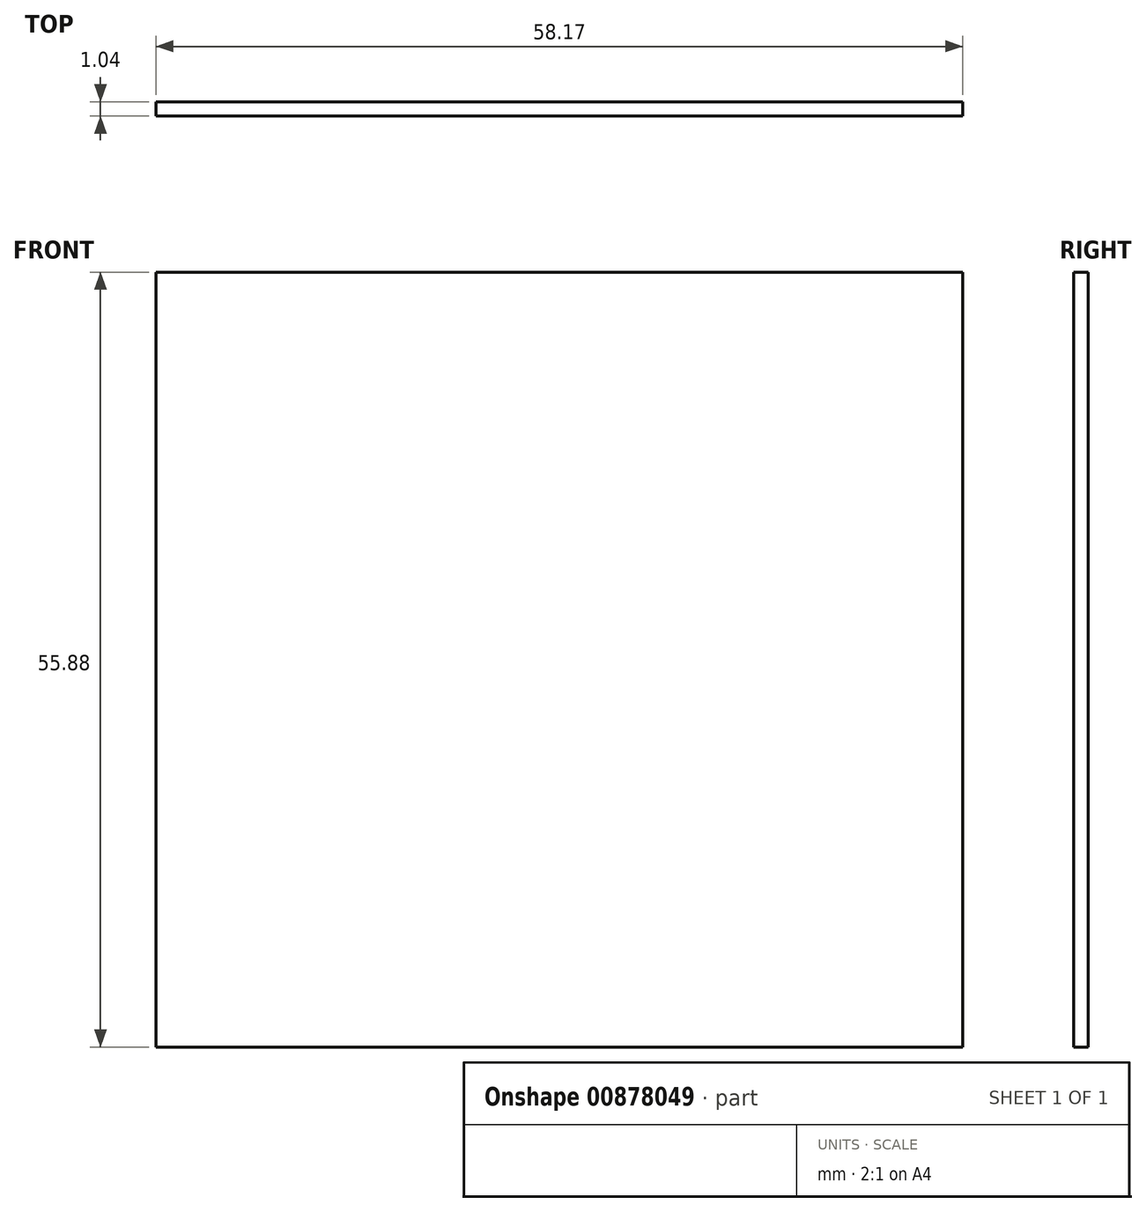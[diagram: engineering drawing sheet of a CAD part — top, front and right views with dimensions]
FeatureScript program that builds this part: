
annotation { "Feature Type Name" : "Feature", "Feature Type Description" : "" }
export const myFeature = defineFeature(function(context is Context, id is Id, definition is map)
    precondition{}
    {
        {
            var Q0;
            Q0=qCreatedBy(makeId("Front.planeOp"),FACE);
            var sketch = newSketch(context, id + "F0", { "sketchPlane" : qUnion([Q0])});
            skLineSegment(sketch, "E0.bottom", {"start": v(0, 0) * mm, "end": v(58.17, 0) * mm});
            skLineSegment(sketch, "E0.top", {"start": v(0, 55.88) * mm, "end": v(58.17, 55.88) * mm});
            skLineSegment(sketch, "E0.left", {"start": v(0, 0) * mm, "end": v(0, 55.88) * mm});
            skLineSegment(sketch, "E0.right", {"start": v(58.17, 0) * mm, "end": v(58.17, 55.88) * mm});
            skSolve(sketch);
        }
        {
            var Q0;
            Q0 = qSketchRegion(id + "F0", true);
            extrude(context, id + "F1", {"entities" : qUnion([Q0]), "depth" : 1.04 * mm, "offsetDistance" : 25.4 * mm});
        }
    });
